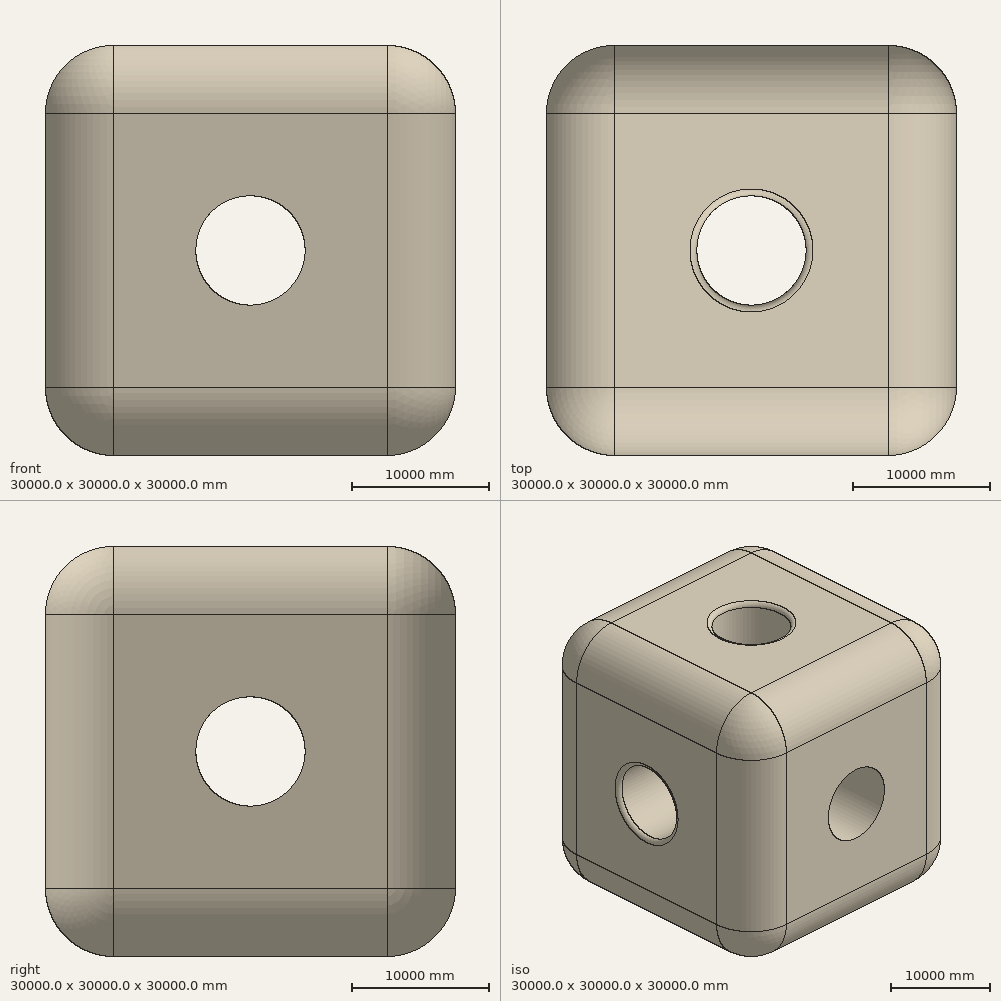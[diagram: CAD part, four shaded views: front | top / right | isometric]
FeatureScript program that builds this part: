
annotation { "Feature Type Name" : "Feature", "Feature Type Description" : "" }
export const myFeature = defineFeature(function(context is Context, id is Id, definition is map)
    precondition{}
    {
        {
            var Q0;
            Q0=qCreatedBy(makeId("Top.planeOp"),FACE);
            var sketch = newSketch(context, id + "F0", { "sketchPlane" : qUnion([Q0])});
            skLineSegment(sketch, "E0.rect.bottom", {"start": v(15000, -15000) * mm, "end": v(-15000, -15000) * mm});
            skLineSegment(sketch, "E0.rect.top", {"start": v(15000, 15000) * mm, "end": v(-15000, 15000) * mm});
            skLineSegment(sketch, "E0.rect.left", {"start": v(15000, -15000) * mm, "end": v(15000, 15000) * mm});
            skLineSegment(sketch, "E0.rect.right", {"start": v(-15000, -15000) * mm, "end": v(-15000, 15000) * mm});
            skPoint(sketch, "E0.rect.middle", {"position": v(0, 0) * mm});
            skSolve(sketch);
        }
        {
            var Q0;
            Q0=makeQuery(id+"F0.imprint","IMPRINT",FACE,{"disambiguationData":[TD([[makeQuery(id+"F0.imprint","IMPRINT",EDGE,{"derivedFrom":sQuery(id+"F0.wireOp",EDGE,"E0.rect.bottom")}),-1.0]])]});
            extrude(context, id + "F1", {"entities" : qUnion([Q0]), "depth" : 30000 * mm, "symmetric" : true});
        }
        {
            var Q0;
            Q0=makeQuery(id+"F1.opExtrude","SWEPT_FACE",FACE,{"disambiguationData":[OSD([sQuery(id+"F0.wireOp",EDGE,"E0.rect.bottom")])]});
            var sketch = newSketch(context, id + "F2", { "sketchPlane" : qUnion([Q0])});
            skCircle(sketch, "E1", {"center": v(0, 0) * mm, "radius": 4000 * mm});
            skSolve(sketch);
        }
        {
            var Q0;
            Q0=makeQuery(id+"F2.imprint","IMPRINT",FACE,{"disambiguationData":[TD([[makeQuery(id+"F2.imprint","IMPRINT",EDGE,{"derivedFrom":sQuery(id+"F2.wireOp",EDGE,"E1")}),1.0]])]});
            extrude(context, id + "F3", {"entities" : qUnion([Q0]), "operationType" : NewBodyOperationType.REMOVE, "endBound" : BoundingType.THROUGH_ALL, "oppositeDirection" : true, "depth" : 25 * mm});
        }
        {
            var Q0;
            Q0=makeQuery(id+"F1.opExtrude","SWEPT_FACE",FACE,{"disambiguationData":[OSD([sQuery(id+"F0.wireOp",EDGE,"E0.rect.left")])]});
            var sketch = newSketch(context, id + "F4", { "sketchPlane" : qUnion([Q0])});
            skCircle(sketch, "E2", {"center": v(0, 0) * mm, "radius": 4000 * mm});
            skSolve(sketch);
        }
        {
            var Q0;
            Q0=makeQuery(id+"F4.imprint","IMPRINT",FACE,{"disambiguationData":[TD([[makeQuery(id+"F4.imprint","IMPRINT",EDGE,{"derivedFrom":sQuery(id+"F4.wireOp",EDGE,"E2")}),1.0]])]});
            extrude(context, id + "F5", {"entities" : qUnion([Q0]), "operationType" : NewBodyOperationType.REMOVE, "endBound" : BoundingType.THROUGH_ALL, "oppositeDirection" : true, "depth" : 25 * mm});
        }
        {
            var Q0;
            Q0=makeQuery(id+"F1.opExtrude","CAP_FACE",FACE,{"disambiguationData":[OSD([sQuery(id+"F0.wireOp",EDGE,"E0.rect.bottom"),sQuery(id+"F0.wireOp",EDGE,"E0.rect.top"),sQuery(id+"F0.wireOp",EDGE,"E0.rect.left"),sQuery(id+"F0.wireOp",EDGE,"E0.rect.right")])],"isStart":true});
            var sketch = newSketch(context, id + "F6", { "sketchPlane" : qUnion([Q0])});
            skCircle(sketch, "E3", {"center": v(0, 0) * mm, "radius": 4000 * mm});
            skSolve(sketch);
        }
        {
            var Q0;
            Q0=makeQuery(id+"F6.imprint","IMPRINT",FACE,{"disambiguationData":[TD([[makeQuery(id+"F6.imprint","IMPRINT",EDGE,{"derivedFrom":sQuery(id+"F6.wireOp",EDGE,"E3")}),1.0]])]});
            extrude(context, id + "F7", {"entities" : qUnion([Q0]), "operationType" : NewBodyOperationType.REMOVE, "endBound" : BoundingType.THROUGH_ALL, "oppositeDirection" : true, "depth" : 25 * mm});
        }
        {
            var Q0;
            Q0=makeQuery(id+"F1.opExtrude","SWEPT_EDGE",EDGE,{"disambiguationData":[OSD([sQuery(id+"F0.wireOp",EDGE,"E0.rect.top"),sQuery(id+"F0.wireOp",EDGE,"E0.rect.left")])]});
            var Q1;
            Q1=makeQuery(id+"F1.opExtrude","CAP_EDGE",EDGE,{"disambiguationData":[OSD([sQuery(id+"F0.wireOp",EDGE,"E0.rect.top")])],"isStart":true});
            var Q2;
            Q2=makeQuery(id+"F1.opExtrude","SWEPT_EDGE",EDGE,{"disambiguationData":[OSD([sQuery(id+"F0.wireOp",EDGE,"E0.rect.top"),sQuery(id+"F0.wireOp",EDGE,"E0.rect.right")])]});
            var Q3;
            Q3=makeQuery(id+"F1.opExtrude","CAP_EDGE",EDGE,{"disambiguationData":[OSD([sQuery(id+"F0.wireOp",EDGE,"E0.rect.top")])],"isStart":false});
            var Q4;
            Q4=makeQuery(id+"F1.opExtrude","CAP_EDGE",EDGE,{"disambiguationData":[OSD([sQuery(id+"F0.wireOp",EDGE,"E0.rect.right")])],"isStart":true});
            var Q5;
            Q5=makeQuery(id+"F1.opExtrude","CAP_EDGE",EDGE,{"disambiguationData":[OSD([sQuery(id+"F0.wireOp",EDGE,"E0.rect.right")])],"isStart":false});
            var Q6;
            Q6=makeQuery(id+"F1.opExtrude","CAP_EDGE",EDGE,{"disambiguationData":[OSD([sQuery(id+"F0.wireOp",EDGE,"E0.rect.left")])],"isStart":true});
            var Q7;
            Q7=makeQuery(id+"F1.opExtrude","CAP_EDGE",EDGE,{"disambiguationData":[OSD([sQuery(id+"F0.wireOp",EDGE,"E0.rect.bottom")])],"isStart":false});
            var Q8;
            Q8=makeQuery(id+"F1.opExtrude","SWEPT_EDGE",EDGE,{"disambiguationData":[OSD([sQuery(id+"F0.wireOp",EDGE,"E0.rect.bottom"),sQuery(id+"F0.wireOp",EDGE,"E0.rect.left")])]});
            var Q9;
            Q9=makeQuery(id+"F1.opExtrude","CAP_EDGE",EDGE,{"disambiguationData":[OSD([sQuery(id+"F0.wireOp",EDGE,"E0.rect.left")])],"isStart":false});
            var Q10;
            Q10=makeQuery(id+"F1.opExtrude","CAP_EDGE",EDGE,{"disambiguationData":[OSD([sQuery(id+"F0.wireOp",EDGE,"E0.rect.bottom")])],"isStart":true});
            var Q11;
            Q11=makeQuery(id+"F1.opExtrude","SWEPT_EDGE",EDGE,{"disambiguationData":[OSD([sQuery(id+"F0.wireOp",EDGE,"E0.rect.bottom"),sQuery(id+"F0.wireOp",EDGE,"E0.rect.right")])]});
            fillet(context, id + "F8", {"entities" : qUnion([Q0, Q1, Q2, Q3, Q4, Q5, Q6, Q7, Q8, Q9, Q10, Q11]), "radius" : 5000 * mm, "tangentPropagation" : true, "allowEdgeOverflow" : false});
        }
        {
            var Q0;
            Q0=makeQuery(id+"F7.boolean.opBoolean","INTERSECT",EDGE,{"derivedFrom":[makeQuery(id+"F1.opExtrude","CAP_FACE",FACE,{"disambiguationData":[OSD([sQuery(id+"F0.wireOp",EDGE,"E0.rect.bottom"),sQuery(id+"F0.wireOp",EDGE,"E0.rect.top"),sQuery(id+"F0.wireOp",EDGE,"E0.rect.left"),sQuery(id+"F0.wireOp",EDGE,"E0.rect.right")])],"isStart":false}),makeQuery(id+"F7.opExtrude","SWEPT_FACE",FACE,{"disambiguationData":[OSD([sQuery(id+"F6.wireOp",EDGE,"E3")])]})]});
            var Q1;
            Q1=makeQuery(id+"F5.boolean.opBoolean","COPY",EDGE,{"derivedFrom":makeQuery(id+"F5.opExtrude","CAP_EDGE",EDGE,{"disambiguationData":[OSD([sQuery(id+"F4.wireOp",EDGE,"E2")])],"isStart":true})});
            var Q2;
            Q2=makeQuery(id+"F3.boolean.opBoolean","INTERSECT",EDGE,{"derivedFrom":[makeQuery(id+"F1.opExtrude","SWEPT_FACE",FACE,{"disambiguationData":[OSD([sQuery(id+"F0.wireOp",EDGE,"E0.rect.top")])]}),makeQuery(id+"F3.opExtrude","SWEPT_FACE",FACE,{"disambiguationData":[OSD([sQuery(id+"F2.wireOp",EDGE,"E1")])]})]});
            var Q3;
            Q3=makeQuery(id+"F7.boolean.opBoolean","COPY",EDGE,{"derivedFrom":makeQuery(id+"F7.opExtrude","CAP_EDGE",EDGE,{"disambiguationData":[OSD([sQuery(id+"F6.wireOp",EDGE,"E3")])],"isStart":true})});
            var Q4;
            Q4=makeQuery(id+"F5.boolean.opBoolean","INTERSECT",EDGE,{"derivedFrom":[makeQuery(id+"F1.opExtrude","SWEPT_FACE",FACE,{"disambiguationData":[OSD([sQuery(id+"F0.wireOp",EDGE,"E0.rect.right")])]}),makeQuery(id+"F5.opExtrude","SWEPT_FACE",FACE,{"disambiguationData":[OSD([sQuery(id+"F4.wireOp",EDGE,"E2")])]})]});
            var Q5;
            Q5=makeQuery(id+"F3.boolean.opBoolean","COPY",EDGE,{"derivedFrom":makeQuery(id+"F3.opExtrude","CAP_EDGE",EDGE,{"disambiguationData":[OSD([sQuery(id+"F2.wireOp",EDGE,"E1")])],"isStart":true})});
            fillet(context, id + "F9", {"entities" : qUnion([Q0, Q1, Q2, Q3, Q4, Q5]), "radius" : 500 * mm, "tangentPropagation" : true, "allowEdgeOverflow" : false});
        }
    });
